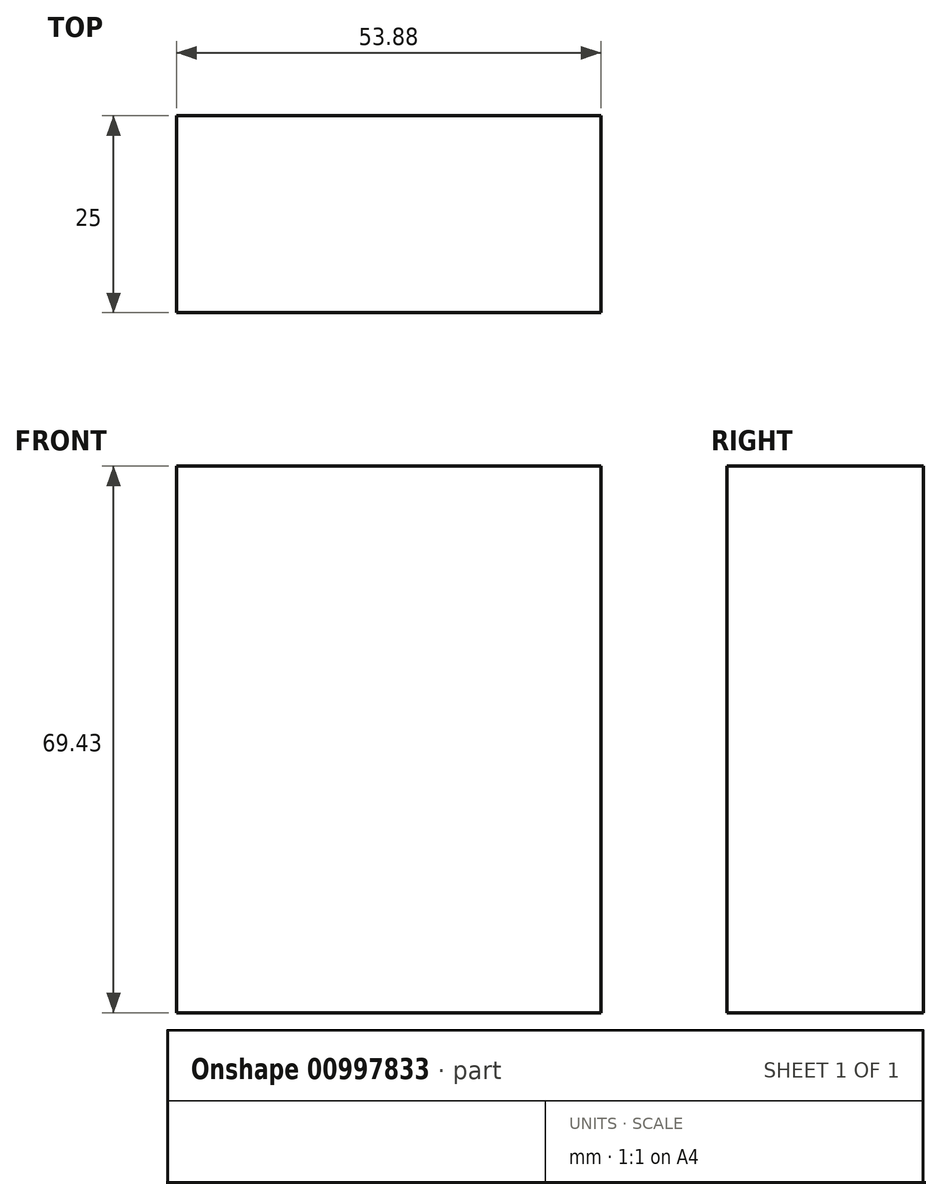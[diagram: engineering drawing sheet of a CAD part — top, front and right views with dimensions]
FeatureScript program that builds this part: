
annotation { "Feature Type Name" : "Feature", "Feature Type Description" : "" }
export const myFeature = defineFeature(function(context is Context, id is Id, definition is map)
    precondition{}
    {
        {
            var Q0;
            Q0=qCreatedBy(makeId("Front.planeOp"),FACE);
            var sketch = newSketch(context, id + "F0", { "sketchPlane" : qUnion([Q0])});
            skLineSegment(sketch, "E0.bottom", {"start": v(-128.69, -5.83) * mm, "end": v(-74.81, -5.83) * mm});
            skLineSegment(sketch, "E0.top", {"start": v(-128.69, 63.6) * mm, "end": v(-74.81, 63.6) * mm});
            skLineSegment(sketch, "E0.left", {"start": v(-128.69, -5.83) * mm, "end": v(-128.69, 63.6) * mm});
            skLineSegment(sketch, "E0.right", {"start": v(-74.81, -5.83) * mm, "end": v(-74.81, 63.6) * mm});
            skPoint(sketch, "E0.middle", {"position": v(-101.75, 28.89) * mm});
            skSolve(sketch);
        }
        {
            var Q0;
            Q0 = qSketchRegion(id + "F0", true);
            extrude(context, id + "F1", {"entities" : qUnion([Q0]), "depth" : 25 * mm, "offsetDistance" : 25 * mm});
        }
    });
